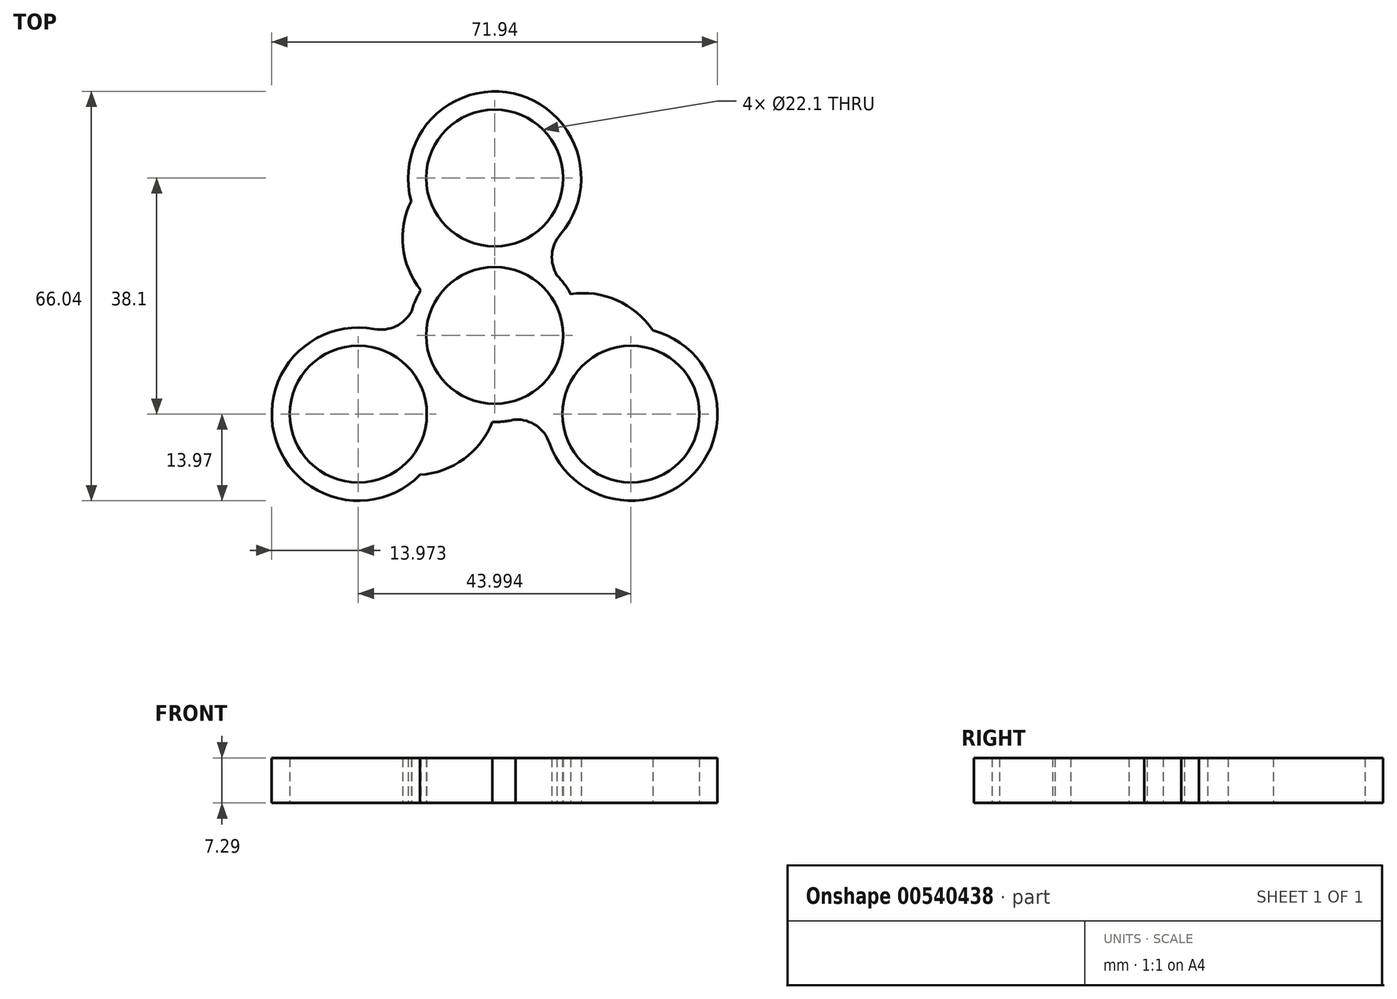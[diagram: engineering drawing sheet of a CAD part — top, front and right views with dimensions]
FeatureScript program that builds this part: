
annotation { "Feature Type Name" : "Feature", "Feature Type Description" : "" }
export const myFeature = defineFeature(function(context is Context, id is Id, definition is map)
    precondition{}
    {
        {
            var Q0;
            Q0=qCreatedBy(makeId("Top.planeOp"),FACE);
            var sketch = newSketch(context, id + "F0", { "sketchPlane" : qUnion([Q0])});
            skPoint(sketch, "E0.center", {"position": v(0, 0) * mm});
            skCircle(sketch, "E1", {"center": v(0, 0) * mm, "radius": 11.05 * mm});
            skCircle(sketch, "E2", {"center": v(0, 0) * mm, "radius": 13.97 * mm});
            skCircle(sketch, "E3", {"center": v(0, 25.4) * mm, "radius": 11.05 * mm});
            skCircle(sketch, "E4.1.0", {"center": v(-22, -12.7) * mm, "radius": 11.05 * mm});
            skCircle(sketch, "E4.2.0", {"center": v(22, -12.7) * mm, "radius": 11.05 * mm});
            skArc(sketch, "E5", {"start": v(-11.05, 25.1) * mm, "mid": v(-14.85, 16.37) * mm, "end": v(-11.91, 7.3) * mm});
            skArc(sketch, "E6.1.0", {"start": v(-16.22, -22.12) * mm, "mid": v(-6.75, -21.04) * mm, "end": v(-0.36, -13.97) * mm});
            skArc(sketch, "E6.2.0", {"start": v(27.27, -2.99) * mm, "mid": v(21.6, 4.68) * mm, "end": v(12.28, 6.67) * mm});
            skCircle(sketch, "E7", {"center": v(0, 25.4) * mm, "radius": 13.97 * mm});
            skCircle(sketch, "E8.1.0", {"center": v(-22, -12.7) * mm, "radius": 13.97 * mm});
            skCircle(sketch, "E8.2.0", {"center": v(22, -12.7) * mm, "radius": 13.97 * mm});
            skArc(sketch, "E9", {"start": v(-19.45, 1.04) * mm, "mid": v(-15.97, 1.47) * mm, "end": v(-13.42, 3.89) * mm});
            skArc(sketch, "E10.1.0", {"start": v(8.83, -17.36) * mm, "mid": v(6.7, -14.56) * mm, "end": v(3.34, -13.56) * mm});
            skArc(sketch, "E10.2.0", {"start": v(10.62, 16.33) * mm, "mid": v(9.26, 13.1) * mm, "end": v(10.07, 9.68) * mm});
            skSolve(sketch);
        }
        {
            var Q0;
            {var subQ1=sQuery(id+"F0.wireOp",EDGE,"E3");var subQ5=sQuery(id+"F0.wireOp",EDGE,"ruSWPlyP-NWsF-Ogou-kngr-VbPYmKv6P5Oa");var subQ8=makeQuery(id+"F0.imprint","INTERSECT",VERTEX,{"disambiguationData":[OD(0.0)],"derivedFrom":[subQ1,subQ5]});Q0=makeQuery(id+"F0.imprint","IMPRINT",FACE,{"disambiguationData":[TD([[makeQuery(id+"F0.imprint","IMPRINT",EDGE,{"disambiguationData":[TD([[subQ8,1.0]])],"derivedFrom":subQ1}),-1.0]])]});}
            var Q1;
            {var subQ5=sQuery(id+"F0.wireOp",EDGE,"0ySpVuuR-PSVZ-cHLL-8CwG-KnoapGbJVRZx");var subQ7=sQuery(id+"F0.wireOp",EDGE,"E2");var subQ8=makeQuery(id+"F0.imprint","INTERSECT",VERTEX,{"derivedFrom":[subQ7,subQ5]});Q1=makeQuery(id+"F0.imprint","IMPRINT",FACE,{"disambiguationData":[TD([[makeQuery(id+"F0.imprint","IMPRINT",EDGE,{"disambiguationData":[TD([[subQ8,-1.0]])],"derivedFrom":subQ7}),-1.0]])]});}
            var Q2;
            {var subQ0=sQuery(id+"F0.wireOp",EDGE,"E7");var subQ7=sQuery(id+"F0.wireOp",EDGE,"E2");var subQ9=makeQuery(id+"F0.imprint","INTERSECT",VERTEX,{"disambiguationData":[OD(0.0)],"derivedFrom":[subQ7,subQ0]});Q2=makeQuery(id+"F0.imprint","IMPRINT",FACE,{"disambiguationData":[TD([[makeQuery(id+"F0.imprint","IMPRINT",EDGE,{"disambiguationData":[TD([[subQ9,-1.0]])],"derivedFrom":subQ7}),-1.0]])]});}
            var Q3;
            Q3=makeQuery(id+"F0.imprint","IMPRINT",FACE,{"disambiguationData":[TD([[makeQuery(id+"F0.imprint","IMPRINT",EDGE,{"derivedFrom":sQuery(id+"F0.wireOp",EDGE,"E1")}),-1.0]])]});
            var Q4;
            {var subQ0=sQuery(id+"F0.wireOp",EDGE,"E8.2.0");var subQ7=sQuery(id+"F0.wireOp",EDGE,"E2");var subQ10=makeQuery(id+"F0.imprint","INTERSECT",VERTEX,{"disambiguationData":[OD(0.0)],"derivedFrom":[subQ7,subQ0]});Q4=makeQuery(id+"F0.imprint","IMPRINT",FACE,{"disambiguationData":[TD([[makeQuery(id+"F0.imprint","IMPRINT",EDGE,{"disambiguationData":[TD([[subQ10,-1.0]])],"derivedFrom":subQ7}),-1.0]])]});}
            var Q5;
            {var subQ1=sQuery(id+"F0.wireOp",EDGE,"E4.2.0");var subQ5=sQuery(id+"F0.wireOp",EDGE,"E6.2.1");var subQ6=makeQuery(id+"F0.imprint","INTERSECT",VERTEX,{"disambiguationData":[OD(0.0)],"derivedFrom":[subQ1,subQ5]});Q5=makeQuery(id+"F0.imprint","IMPRINT",FACE,{"disambiguationData":[TD([[makeQuery(id+"F0.imprint","IMPRINT",EDGE,{"disambiguationData":[TD([[subQ6,1.0]])],"derivedFrom":subQ1}),-1.0]])]});}
            var Q6;
            {var subQ1=sQuery(id+"F0.wireOp",EDGE,"E6.1.1");var subQ3=sQuery(id+"F0.wireOp",EDGE,"E4.1.0");var subQ7=makeQuery(id+"F0.imprint","INTERSECT",VERTEX,{"disambiguationData":[OD(0.0)],"derivedFrom":[subQ3,subQ1]});Q6=makeQuery(id+"F0.imprint","IMPRINT",FACE,{"disambiguationData":[TD([[makeQuery(id+"F0.imprint","IMPRINT",EDGE,{"disambiguationData":[TD([[subQ7,1.0]])],"derivedFrom":subQ3}),-1.0]])]});}
            var Q7;
            {var subQ0=sQuery(id+"F0.wireOp",EDGE,"E8.1.0");var subQ8=sQuery(id+"F0.wireOp",EDGE,"E2");var subQ9=makeQuery(id+"F0.imprint","INTERSECT",VERTEX,{"disambiguationData":[OD(0.0)],"derivedFrom":[subQ8,subQ0]});Q7=makeQuery(id+"F0.imprint","IMPRINT",FACE,{"disambiguationData":[TD([[makeQuery(id+"F0.imprint","IMPRINT",EDGE,{"disambiguationData":[TD([[subQ9,-1.0]])],"derivedFrom":subQ8}),-1.0]])]});}
            var Q8;
            {var subQ0=sQuery(id+"F0.wireOp",EDGE,"E5");var subQ1=sQuery(id+"F0.wireOp",EDGE,"E2");var subQ2=makeQuery(id+"F0.imprint","INTERSECT",VERTEX,{"derivedFrom":[subQ1,subQ0]});Q8=makeQuery(id+"F0.imprint","IMPRINT",FACE,{"disambiguationData":[TD([[makeQuery(id+"F0.imprint","IMPRINT",EDGE,{"disambiguationData":[TD([[subQ2,1.0]])],"derivedFrom":subQ1}),-1.0]])]});}
            var Q9;
            {var subQ0=sQuery(id+"F0.wireOp",EDGE,"0ySpVuuR-PSVZ-cHLL-8CwG-KnoapGbJVRZx");var subQ1=sQuery(id+"F0.wireOp",EDGE,"E2");var subQ2=makeQuery(id+"F0.imprint","INTERSECT",VERTEX,{"derivedFrom":[subQ1,subQ0]});Q9=makeQuery(id+"F0.imprint","IMPRINT",FACE,{"disambiguationData":[TD([[makeQuery(id+"F0.imprint","IMPRINT",EDGE,{"disambiguationData":[TD([[subQ2,-1.0]])],"derivedFrom":subQ1}),1.0]])]});}
            var Q10;
            {var subQ0=sQuery(id+"F0.wireOp",EDGE,"E8.1.0");var subQ1=sQuery(id+"F0.wireOp",EDGE,"E2");var subQ2=makeQuery(id+"F0.imprint","INTERSECT",VERTEX,{"disambiguationData":[OD(0.0)],"derivedFrom":[subQ1,subQ0]});Q10=makeQuery(id+"F0.imprint","IMPRINT",FACE,{"disambiguationData":[TD([[makeQuery(id+"F0.imprint","IMPRINT",EDGE,{"disambiguationData":[TD([[subQ2,-1.0]])],"derivedFrom":subQ1}),1.0]])]});}
            var Q11;
            {var subQ0=sQuery(id+"F0.wireOp",EDGE,"E7");var subQ1=sQuery(id+"F0.wireOp",EDGE,"E2");var subQ2=makeQuery(id+"F0.imprint","INTERSECT",VERTEX,{"disambiguationData":[OD(0.0)],"derivedFrom":[subQ1,subQ0]});Q11=makeQuery(id+"F0.imprint","IMPRINT",FACE,{"disambiguationData":[TD([[makeQuery(id+"F0.imprint","IMPRINT",EDGE,{"disambiguationData":[TD([[subQ2,-1.0]])],"derivedFrom":subQ1}),1.0]])]});}
            var Q12;
            {var subQ0=sQuery(id+"F0.wireOp",EDGE,"E6.2.0");var subQ1=sQuery(id+"F0.wireOp",EDGE,"E2");var subQ2=makeQuery(id+"F0.imprint","INTERSECT",VERTEX,{"derivedFrom":[subQ1,subQ0]});Q12=makeQuery(id+"F0.imprint","IMPRINT",FACE,{"disambiguationData":[TD([[makeQuery(id+"F0.imprint","IMPRINT",EDGE,{"disambiguationData":[TD([[subQ2,1.0]])],"derivedFrom":subQ1}),-1.0]])]});}
            var Q13;
            {var subQ0=sQuery(id+"F0.wireOp",EDGE,"E8.2.0");var subQ1=sQuery(id+"F0.wireOp",EDGE,"E2");var subQ2=makeQuery(id+"F0.imprint","INTERSECT",VERTEX,{"disambiguationData":[OD(0.0)],"derivedFrom":[subQ1,subQ0]});Q13=makeQuery(id+"F0.imprint","IMPRINT",FACE,{"disambiguationData":[TD([[makeQuery(id+"F0.imprint","IMPRINT",EDGE,{"disambiguationData":[TD([[subQ2,-1.0]])],"derivedFrom":subQ1}),1.0]])]});}
            var Q14;
            {var subQ0=sQuery(id+"F0.wireOp",EDGE,"E6.2.1");var subQ1=sQuery(id+"F0.wireOp",EDGE,"E2");var subQ2=makeQuery(id+"F0.imprint","INTERSECT",VERTEX,{"derivedFrom":[subQ1,subQ0]});Q14=makeQuery(id+"F0.imprint","IMPRINT",FACE,{"disambiguationData":[TD([[makeQuery(id+"F0.imprint","IMPRINT",EDGE,{"disambiguationData":[TD([[subQ2,-1.0]])],"derivedFrom":subQ1}),-1.0]])]});}
            var Q15;
            {var subQ0=sQuery(id+"F0.wireOp",EDGE,"E6.1.0");var subQ1=sQuery(id+"F0.wireOp",EDGE,"E2");var subQ2=makeQuery(id+"F0.imprint","INTERSECT",VERTEX,{"derivedFrom":[subQ1,subQ0]});Q15=makeQuery(id+"F0.imprint","IMPRINT",FACE,{"disambiguationData":[TD([[makeQuery(id+"F0.imprint","IMPRINT",EDGE,{"disambiguationData":[TD([[subQ2,1.0]])],"derivedFrom":subQ1}),-1.0]])]});}
            var Q16;
            {var subQ0=sQuery(id+"F0.wireOp",EDGE,"E6.1.1");var subQ1=sQuery(id+"F0.wireOp",EDGE,"E2");var subQ2=makeQuery(id+"F0.imprint","INTERSECT",VERTEX,{"derivedFrom":[subQ1,subQ0]});Q16=makeQuery(id+"F0.imprint","IMPRINT",FACE,{"disambiguationData":[TD([[makeQuery(id+"F0.imprint","IMPRINT",EDGE,{"disambiguationData":[TD([[subQ2,-1.0]])],"derivedFrom":subQ1}),-1.0]])]});}
            var Q17;
            {var subQ0=sQuery(id+"F0.wireOp",EDGE,"ruSWPlyP-NWsF-Ogou-kngr-VbPYmKv6P5Oa");var subQ1=sQuery(id+"F0.wireOp",EDGE,"E2");var subQ2=makeQuery(id+"F0.imprint","INTERSECT",VERTEX,{"derivedFrom":[subQ1,subQ0]});Q17=makeQuery(id+"F0.imprint","IMPRINT",FACE,{"disambiguationData":[TD([[makeQuery(id+"F0.imprint","IMPRINT",EDGE,{"disambiguationData":[TD([[subQ2,-1.0]])],"derivedFrom":subQ1}),-1.0]])]});}
            extrude(context, id + "F1", {"entities" : qUnion([Q0, Q1, Q2, Q3, Q4, Q5, Q6, Q7, Q8, Q9, Q10, Q11, Q12, Q13, Q14, Q15, Q16, Q17]), "depth" : 7.3 * mm, "offsetDistance" : 25.4 * mm});
        }
    });
